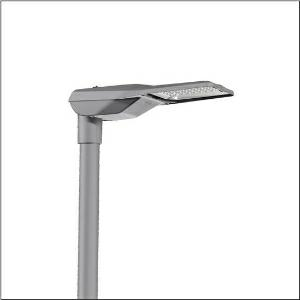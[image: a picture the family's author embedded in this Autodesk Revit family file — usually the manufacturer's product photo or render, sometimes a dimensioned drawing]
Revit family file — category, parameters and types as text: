
# Revit family: streetlight_sl_21_mini___pl52_5xe2h43s08gb_8da4
name_source: partatom
category: Lighting Fixtures
units: mm (PartAtom-declared; Revit-internal decimal feet)

## family parameters
Cut with Voids When Loaded = No
Host = Face
Light Source = No
Part Type = Normal
Room Calculation Point = No
Round Connector Dimension = Use Diameter
Shared = No

## types (1)
- --- (1 x LED, 6080 lm, 40.4 W, 4000K)
    Apparent Load = 40 VA
    CIE Flux Codes = 27 59 98 100 100
    Color Rendering = 70
    Color Temperature = 4000K
    Default Elevation = 1800 mm
    Description = Streetlight SL 21 mini, mast luminaire, primary light control with lens, of PMMA, primary optical cover: cover, of toughened safety glass, transparent, light distribution: PL52, light emission: direct distribution, primary light characteristic: asymmetric, installation type: side-entry, post-top, LED, High Power LED, rated luminous flux: 6.080lm, luminous efficacy: 151lm/W, light colour: 740, colour temperature: 4000K, control gear: D4i, control: overheat protection, constant luminous flux control, time-dependent luminous flux control, flexible luminous flux parameterisation, pre-setting: logarithmic dimming characteristic, mains connection: 220..240V, AC, 50/60Hz, start of lifetime: 40W, end of service life: 41W, reduction: 19W, luminaire housing, of diecast aluminium, powder-coated, Siteco® metallic grey (DB 702S), corrosivity category C5 mid according to DIN EN ISO 12944, please order mast flange separately, inclination adjustable: 0°, 5°, 10°, 15°, sealing non-destructively replaceable, multi-level sealing system, length: 628mm, width: 235mm, height: 110mm, mast flange for spigot size: 42mm (side-entry): 5XC10008XM4, 60/48mm (side-entry/post-top): 5XC10108XM2, 76/60mm (side-entry/post-top): 5XC10108XM1, mounting height: 4..8m, Smart Interface above, protection rating (complete): IP66, insulation class (complete): insulation class II (safety insulation), certification: CE, ENEC, ENEC+, VDE, impact resistance: IK10, permissible operating ambient temperature for outdoor applications: -40..+50°C, standard-compliant lighting for roads and squares, packaging unit: 1 piece

Light Distribution: PL52
    Height = 110 mm
    Lamp = 1 x LED
    Lamp Light Flux = 6080 lm
    Lamp Power = 40.4 W
    Lamp count = 1
    Length = 625 mm
    Luminous efficacy = 151 lm/W
    Manufacturer = Siteco
    ModVariant = No
    Model = 5XE2H43S08GB
    Number of Poles = 1
    OnlyDefault = Yes
    Power Factor = 1
    Product Name = Streetlight SL 21 mini | PL52
    Product group = mast luminaire | pylon top
    ProductGroupID = 6100
    Protection Class = Protection class II
    Protection Degree = IP 66
    RLX_Detail_Level = 1
    RLX_Emergency_Light_Flux = 0 lm
    RLX_Emergency_Type = 0
    RLX_Emergency_Type_DB = No
    RlxData = <blob elided: 35717 chars, md5=a0de3370>
    Socket = socket
    Standby Power = 0 W
    System Light Flux = 6080 lm
    System Power = 40 W
    Type Comments = factory setting: luminous flux: 100 % | dim-lin: 254 | 812 mA
    Type Image = l_1003515.jpg
    URL = http://relux.com
    VarID = @adj_190166
    Voltage = 0 V
    Weight = 0.00 kg
    Width = 234 mm

## geometry (parser evidence)
native form markers: Blend x4, Sweep x11
no freeform markers — native parametric forms only
